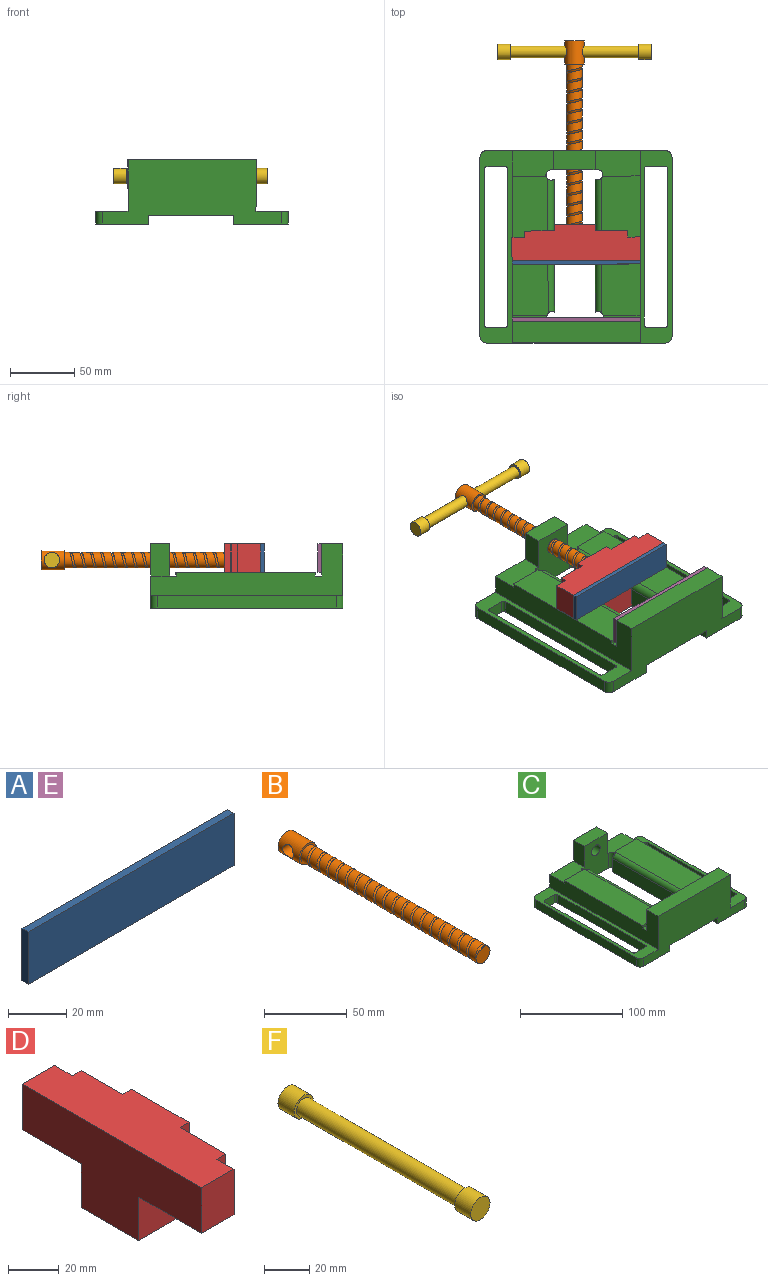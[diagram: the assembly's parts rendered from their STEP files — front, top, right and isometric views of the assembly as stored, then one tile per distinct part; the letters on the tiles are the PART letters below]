
ASSEMBLY  parts=6 mates=4
PART A: 6 faces, bbox 100x3x22 mm
  f0: plane 22x3mm, normal (-1,0,0), area 66mm2, adj f1,f3,f4,f5
  f1: plane 100x3mm, normal (0,0,-1), area 300mm2, adj f0,f2,f4,f5
  f2: plane 22x3mm, normal (1,0,0), area 66mm2, adj f1,f3,f4,f5
  f3: plane 100x3mm, normal (0,0,1), area 300mm2, adj f0,f2,f4,f5
  f4: plane 100x22mm, normal (0,-1,0), area 2200mm2, adj f0,f1,f2,f3
  f5: plane 100x22mm, normal (0,1,0), area 2200mm2, adj f0,f1,f2,f3
PART B: 9 faces, bbox 15.4x170.1x15.3 mm
  f0: cylinder r=7.5mm len=18mm, axis (0,-1,0), area 714.5mm2, adj f6,f7,f8
  f1: cylinder r=6mm len=150mm, axis (0,1,0), area 4100.7mm2, adj f2,f3,f4,f5,f7
  f2: plane 12.35x12.35mm, normal (0,-1,0), area 109.3mm2, adj f1,f4,f5
  f3: plane 1.73x1mm, normal (1,0,0), area 0.9mm2, adj f1,f4,f5
  f4: bspline ~151.73x12mm, area 1298.2mm2, adj f1,f2,f3,f5
  f5: bspline ~149x14mm, area 658mm2, adj f1,f2,f3,f4
  f6: plane 15x15mm, normal (0,1,0), area 176.7mm2, adj f0
  f7: plane 15x15mm, normal (0,-1,0), area 63.6mm2, adj f0,f1
  f8: cylinder r=4.5mm len=15mm, axis (1,0,0), area 382.8mm2, adj f0
PART C: 61 faces, bbox 149.9x150.1x50.1 mm
  f0: plane 150x42.5mm, normal (0,0,-1), area 4101.7mm2, adj f3,f19,f23,f34,f45,f46,f47,f48
  f1: plane 103.69x15.95mm, normal (-1,0,0), area 1654.2mm2, adj f8,f9,f36,f59
  f2: plane 103.68x15.95mm, normal (1,0,0), area 1654.1mm2, adj f6,f7,f36,f60
  f3: plane 139.79x50mm, normal (0,-1,0), area 4929mm2, adj f0,f13,f16,f17,f18,f20,f21,f34
  f4: plane 43.02x36.31mm, normal (0,-1,0), area 1337.6mm2, adj f7,f9,f12,f14,f15,f24,f25,f26
  f5: plane 100x42.95mm, normal (0,1,0), area 3144.6mm2, adj f6,f8,f10,f11,f16,f17,f18,f36
  f6: cylinder r=4mm len=20.95mm, axis (0,0,1), area 278.8mm2, adj f2,f5,f11,f28,f29,f36,f60
  f7: cylinder r=4mm len=20.95mm, axis (0,0,1), area 285mm2, adj f2,f4,f14,f27,f29,f36,f60
  f8: cylinder r=4mm len=20.95mm, axis (0,0,1), area 280.2mm2, adj f1,f5,f10,f31,f33,f36,f59
  f9: cylinder r=4mm len=20.95mm, axis (0,0,1), area 279.5mm2, adj f1,f4,f12,f30,f33,f36,f59
  f10: plane 32.68x5.17mm, normal (0,0,1), area 150mm2, adj f5,f8,f18,f31
  f11: plane 31.18x5.02mm, normal (0,0,1), area 139.9mm2, adj f5,f6,f16,f28
  f12: plane 35.16x19.88mm, normal (0,0,1), area 670.6mm2, adj f4,f9,f18,f23,f24,f30
  f13: plane 150x41.36mm, normal (0,0,-1), area 3936.1mm2, adj f3,f22,f23,f35,f37,f38,f39,f40
  f14: plane 32.71x20.2mm, normal (0,0,1), area 631.9mm2, adj f4,f7,f16,f23,f25,f27
  f15: plane 32x15mm, normal (0,0,1), area 478mm2, adj f4,f23,f24,f25
  f16: plane 150x40mm, normal (-1,0,0), area 2987.9mm2, adj f3,f5,f11,f14,f17,f21,f23,f27
  f17: plane 100x16.52mm, normal (0,0,1), area 1652.3mm2, adj f3,f5,f16,f18
  f18: plane 150x40mm, normal (1,0,-0.01), area 2663.1mm2, adj f3,f5,f10,f12,f17,f20,f23,f32
  f19: plane 140x10mm, normal (1,0,0), area 1400mm2, adj f0,f20,f56,f58
  f20: plane 150x25mm, normal (0,0,1), area 1477.1mm2, adj f3,f18,f19,f23,f45,f46,f47,f48
  f21: plane 150x25mm, normal (0,0,1), area 1482.8mm2, adj f3,f16,f22,f23,f37,f38,f39,f40
  f22: plane 140x10mm, normal (-1,0,0), area 1400mm2, adj f13,f21,f55,f57
  f23: plane 139.79x50mm, normal (0,1,0), area 3117.5mm2, adj f0,f12,f13,f14,f15,f16,f18,f20
  f24: plane 25x14.87mm, normal (1,0,0), area 371.8mm2, adj f4,f12,f15,f23
  f25: plane 25x15mm, normal (-1,0,0), area 375mm2, adj f4,f14,f15,f23
  f26: cylinder r=6mm len=14.94mm, axis (0,1,0), area 562.6mm2, adj f4,f23
  f27: plane 26.66x3mm, normal (0,1,0), area 80mm2, adj f7,f14,f16,f29
  f28: plane 27.32x3mm, normal (0,-1,0), area 81.9mm2, adj f6,f11,f16,f29
  f29: plane 108.26x28.16mm, normal (0,0,1), area 3023.8mm2, adj f6,f7,f16,f27,f28,f60
  f30: plane 29.27x3mm, normal (0,1,0), area 87.8mm2, adj f9,f12,f32,f33
  f31: plane 28.82x3mm, normal (0,-1,0), area 86.5mm2, adj f8,f10,f32,f33
  f32: plane 108.54x3mm, normal (1,0,0), area 325.6mm2, adj f18,f30,f31,f33
  f33: plane 108.66x30.13mm, normal (0,0,1), area 3245.7mm2, adj f8,f9,f30,f31,f32,f59
  f34: plane 150x7.05mm, normal (-1,0,0), area 1057mm2, adj f0,f3,f23,f36
  f35: plane 150x7.05mm, normal (1,0,0), area 1057mm2, adj f3,f13,f23,f36
  f36: plane 150x65.93mm, normal (0,0,-1), area 5931.7mm2, adj f1,f2,f3,f4,f5,f6,f7,f8
  f37: plane 14x10mm, normal (0,1,0), area 140mm2, adj f13,f21,f38,f44
  f38: cylinder r=2mm len=10mm, axis (0,0,1), area 31.8mm2, adj f13,f21,f37,f39
  f39: plane 121.39x10mm, normal (-1,0,0), area 1213.9mm2, adj f13,f21,f38,f40
  f40: cylinder r=2mm len=10mm, axis (0,0,1), area 33mm2, adj f13,f21,f39,f41
  f41: plane 14x10mm, normal (0,-1,0), area 140mm2, adj f13,f21,f40,f42
  f42: cylinder r=2mm len=10mm, axis (0,0,1), area 32.5mm2, adj f13,f21,f41,f43
  f43: plane 121.43x10mm, normal (1,0,0), area 1214.3mm2, adj f13,f21,f42,f44
  f44: cylinder r=2mm len=10mm, axis (0,0,1), area 31.9mm2, adj f13,f21,f37,f43
  f45: plane 59.83x10mm, normal (1,0,0), area 598.3mm2, adj f0,f20,f46,f54
  f46: plane 48.46x10mm, normal (1,0,0), area 484.6mm2, adj f0,f20,f45,f47
  f47: plane 14.03x10mm, normal (1,0,0), area 140.3mm2, adj f0,f20,f46,f48
  f48: cylinder r=2mm len=10mm, axis (0,0,1), area 28.5mm2, adj f0,f20,f47,f49
  f49: plane 14x10mm, normal (0,1,0), area 140mm2, adj f0,f20,f48,f50
  f50: cylinder r=2mm len=10mm, axis (0,0,1), area 32mm2, adj f0,f20,f49,f51
  f51: plane 122.32x10mm, normal (-1,0,0), area 1223.2mm2, adj f0,f20,f50,f52
  f52: cylinder r=2mm len=10mm, axis (0,0,1), area 27.6mm2, adj f0,f20,f51,f53
  f53: plane 14x10mm, normal (0,-1,0), area 140mm2, adj f0,f20,f52,f54
  f54: cylinder r=2mm len=10mm, axis (0,0,1), area 31.2mm2, adj f0,f20,f45,f53
  f55: cylinder r=5mm len=10mm, axis (0,0,-1), area 78.5mm2, adj f13,f21,f22,f23
  f56: cylinder r=5mm len=10mm, axis (0,0,1), area 78.5mm2, adj f0,f19,f20,f23
  f57: cylinder r=5mm len=10mm, axis (0,0,1), area 78.5mm2, adj f3,f13,f21,f22
  f58: cylinder r=5mm len=10mm, axis (0,0,-1), area 78.5mm2, adj f0,f3,f19,f20
  f59: cylinder r=5mm len=105.32mm, axis (0,-1,0), area 811mm2, adj f1,f8,f9,f33
  f60: cylinder r=5mm len=104.96mm, axis (0,1,0), area 810mm2, adj f2,f6,f7,f29
PART D: 18 faces, bbox 28x100x43 mm
  f0: plane 23x22mm, normal (1,0,0), area 506mm2, adj f6,f7,f9,f13
  f1: plane 22x10mm, normal (1,0,0), area 220mm2, adj f7,f8,f9,f13
  f2: plane 22x18mm, normal (0,-1,0), area 396mm2, adj f3,f9,f10,f11
  f3: plane 35x23mm, normal (0,0,-1), area 757.4mm2, adj f2,f4,f10,f11,f12,f14
  f4: plane 43x28mm, normal (0,-1,0), area 698mm2, adj f3,f5,f9,f10,f14,f15
  f5: plane 32x28mm, normal (0,0,-1), area 896mm2, adj f4,f6,f10,f15
  f6: plane 43x28mm, normal (0,1,0), area 698mm2, adj f0,f5,f7,f9,f10,f15
  f7: plane 33x23mm, normal (0,0,-1), area 709mm2, adj f0,f1,f6,f8,f10,f13
  f8: plane 22x18mm, normal (0,1,0), area 396mm2, adj f1,f7,f9,f10
  f9: plane 100x28mm, normal (0,0,1), area 2362.4mm2, adj f0,f1,f2,f4,f6,f8,f10,f11
  f10: plane 100x43mm, normal (-1,0,0), area 2872mm2, adj f2,f3,f4,f5,f6,f7,f8,f9
  f11: plane 22x9.52mm, normal (1,0,0), area 209.4mm2, adj f2,f3,f9,f12
  f12: plane 22x5mm, normal (0,-1,0), area 110mm2, adj f3,f9,f11,f14
  f13: plane 22x5mm, normal (0,1,0), area 110mm2, adj f0,f1,f7,f9
  f14: plane 25.48x22mm, normal (1,0,0), area 560.6mm2, adj f3,f4,f9,f12
  f15: plane 43x32mm, normal (1,0,0), area 1262.9mm2, adj f4,f5,f6,f9,f16
  f16: cylinder r=6mm len=25mm, axis (1,0,0), area 942.5mm2, adj f15,f17
  f17: plane 12x12mm, normal (1,0,0), area 113.1mm2, adj f16
PART E: same geometry as A
PART F: 7 faces, bbox 12x120x12 mm
  f0: cylinder r=4.5mm len=100mm, axis (0,1,0), area 2827.4mm2, adj f3,f6
  f1: cylinder r=6mm len=12mm, axis (0,1,0), area 377mm2, adj f2,f3
  f2: plane 12x12mm, normal (0,-1,0), area 113.1mm2, adj f1
  f3: plane 12x12mm, normal (0,1,0), area 49.5mm2, adj f0,f1
  f4: cylinder r=6mm len=12mm, axis (0,-1,0), area 377mm2, adj f5,f6
  f5: plane 12x12mm, normal (0,1,0), area 113.1mm2, adj f4
  f6: plane 12x12mm, normal (0,-1,0), area 49.5mm2, adj f0,f4
PLACE A rot(axis=(0,0,1),0.2deg) t=(83.85,55.2,90.72)mm
PLACE B rot(axis=(-1,0,0),0deg) t=(93.81,208.31,100.1)mm
PLACE C rot(axis=(-1,0,0),0deg) t=(94.81,140.83,72.72)mm
PLACE D rot(axis=(0,0,1),90.2deg) t=(95.02,73.25,74.62)mm
PLACE E rot(axis=(-1,0,0),0deg) t=(83.86,10.35,90.72)mm
PLACE F rot(axis=(0,0,1),90deg) t=(43.81,217.86,100.1)mm
MATE fastened B.f1 <-> C.f26  axis (0,1,0) through (93.81,133.31,100.1)mm
MATE fastened E.f4 <-> C.f5  axis (0,-1,0) through (95.1,7.35,112.72)mm
MATE fastened F.f0 <-> B.f8  axis (-1,0,0) through (93.81,217.86,100.1)mm
MATE fastened A.f5 <-> D.f10  axis (0,1,0) through (95.1,55.25,112.72)mm
